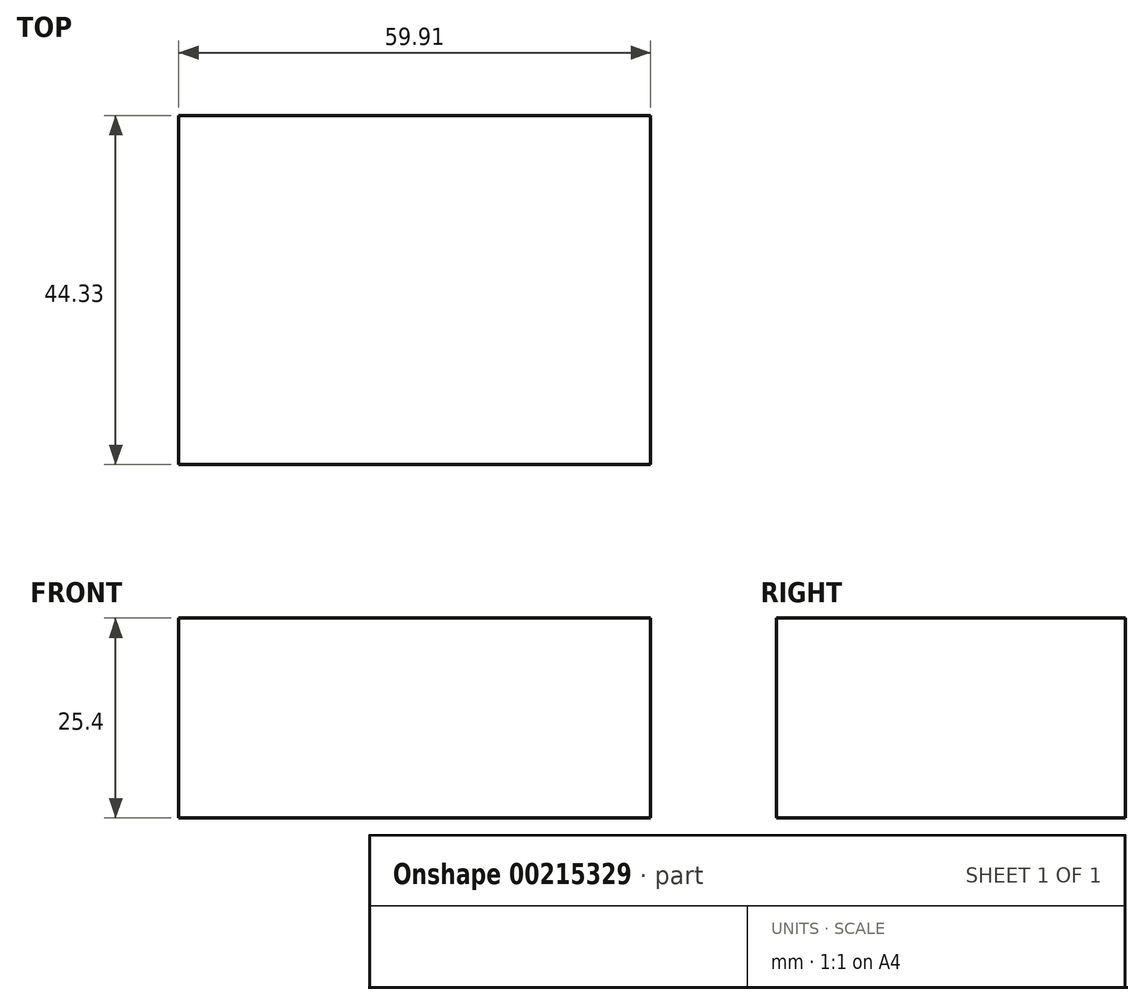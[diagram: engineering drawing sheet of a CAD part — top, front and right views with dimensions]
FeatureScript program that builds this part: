
annotation { "Feature Type Name" : "Feature", "Feature Type Description" : "" }
export const myFeature = defineFeature(function(context is Context, id is Id, definition is map)
    precondition{}
    {
        {
            var Q0;
            Q0=qCreatedBy(makeId("Top.planeOp"),FACE);
            var sketch = newSketch(context, id + "F0", { "sketchPlane" : qUnion([Q0])});
            skLineSegment(sketch, "E0.bottom", {"start": v(-45.34, 34.26) * mm, "end": v(14.57, 34.26) * mm});
            skLineSegment(sketch, "E0.top", {"start": v(-45.34, -10.07) * mm, "end": v(14.57, -10.07) * mm});
            skLineSegment(sketch, "E0.left", {"start": v(-45.34, 34.26) * mm, "end": v(-45.34, -10.07) * mm});
            skLineSegment(sketch, "E0.right", {"start": v(14.57, 34.26) * mm, "end": v(14.57, -10.07) * mm});
            skSolve(sketch);
        }
        {
            var Q0;
            Q0 = qSketchRegion(id + "F0", true);
            extrude(context, id + "F1", {"entities" : qUnion([Q0]), "depth" : 25.4 * mm});
        }
    });
